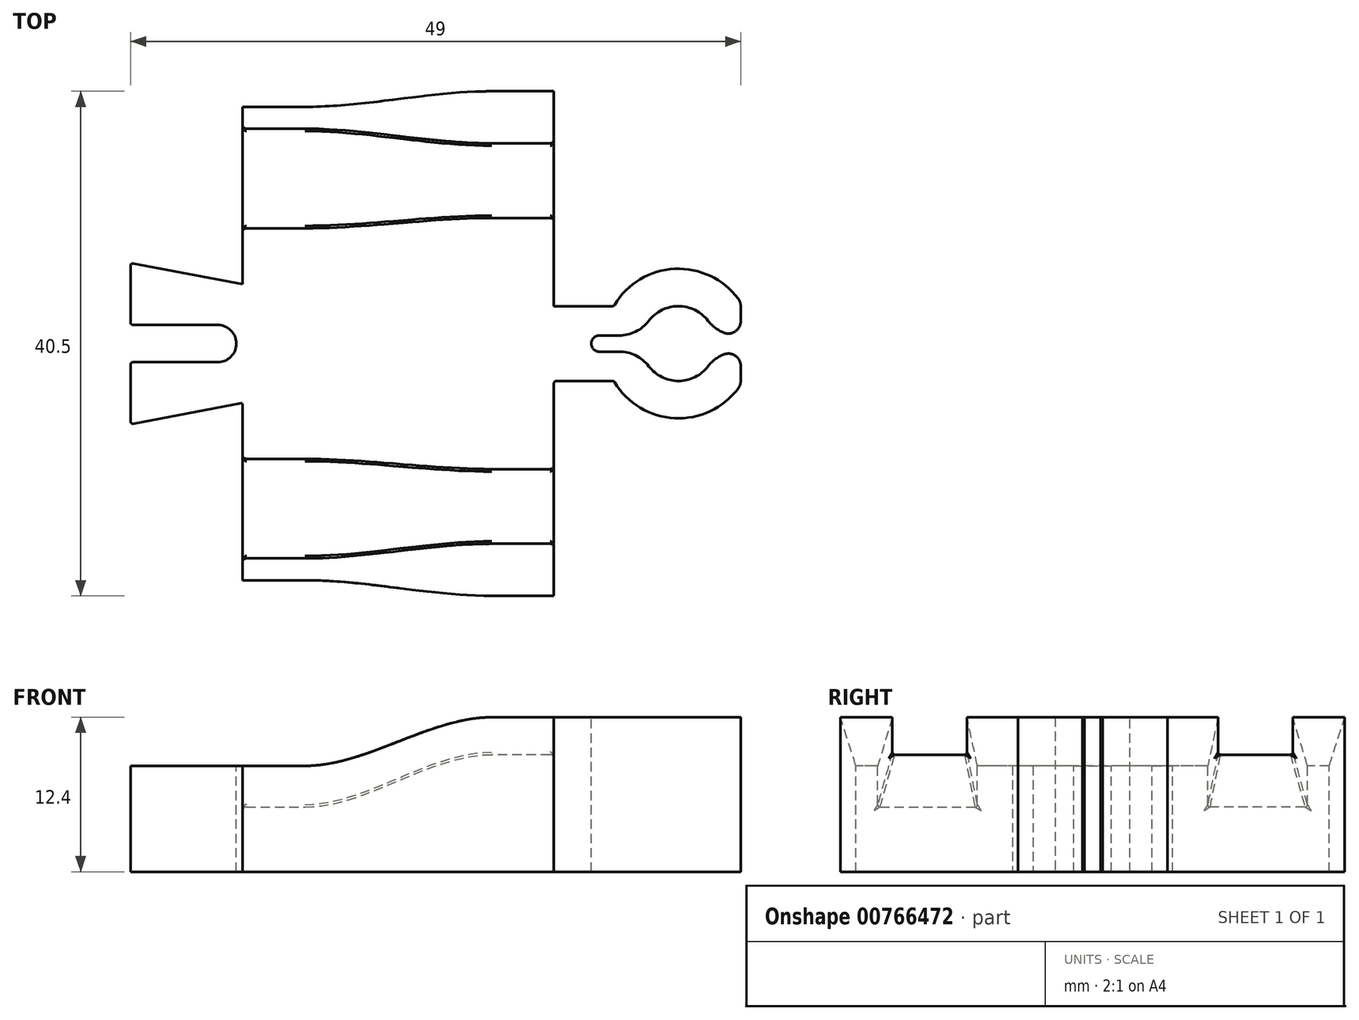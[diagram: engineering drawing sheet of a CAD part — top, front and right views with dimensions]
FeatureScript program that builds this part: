
annotation { "Feature Type Name" : "Feature", "Feature Type Description" : "" }
export const myFeature = defineFeature(function(context is Context, id is Id, definition is map)
    precondition{}
    {
        {
            var Q0;
            Q0=qCreatedBy(makeId("Right.planeOp"),FACE);
            cPlane(context, id + "F0", {"entities" : qUnion([Q0]), "cplaneType" : CPlaneType.OFFSET, "offset" : 15 * mm, "width" : 150 * mm, "height" : 150 * mm});
        }
        {
            var Q0;
            Q0=qCreatedBy(makeId("Right.planeOp"),FACE);
            var sketch = newSketch(context, id + "F1", { "sketchPlane" : qUnion([Q0])});
            skLineSegment(sketch, "E0.bottom", {"start": v(19, 0) * mm, "end": v(-19, 0) * mm});
            skLineSegment(sketch, "E0.top", {"start": v(19, 8.5) * mm, "end": v(17.25, 8.5) * mm});
            skLineSegment(sketch, "E0.left", {"start": v(19, 0) * mm, "end": v(19, 8.5) * mm});
            skLineSegment(sketch, "E0.right", {"start": v(-19, 0) * mm, "end": v(-19, 8.5) * mm});
            skPoint(sketch, "E0.middle", {"position": v(0, 4.25) * mm});
            skLineSegment(sketch, "E1.bottom", {"start": v(17.25, 5.2) * mm, "end": v(9.25, 5.2) * mm});
            skLineSegment(sketch, "E1.left", {"start": v(17.25, 5.2) * mm, "end": v(17.25, 8.5) * mm});
            skLineSegment(sketch, "E1.right", {"start": v(9.25, 5.2) * mm, "end": v(9.25, 8.5) * mm});
            skPoint(sketch, "E1.middle", {"position": v(13.25, 12.03) * mm});
            skPoint(sketch, "E2.orphan", {"position": v(9.25, 18.86) * mm});
            skPoint(sketch, "E3.orphan", {"position": v(17.25, 18.86) * mm});
            skLineSegment(sketch, "E4.trimOffspring", {"start": v(9.25, 8.5) * mm, "end": v(-9.25, 8.5) * mm});
            skLineSegment(sketch, "E5.MirrorCS", {"start": v(-9.25, 5.2) * mm, "end": v(-9.25, 8.5) * mm});
            skLineSegment(sketch, "E6.MirrorCS", {"start": v(-17.25, 5.2) * mm, "end": v(-9.25, 5.2) * mm});
            skLineSegment(sketch, "E7.MirrorCS", {"start": v(-17.25, 5.2) * mm, "end": v(-17.25, 8.5) * mm});
            skLineSegment(sketch, "E8.trimOffspring", {"start": v(-17.25, 8.5) * mm, "end": v(-19, 8.5) * mm});
            skSolve(sketch);
        }
        {
            var Q0;
            Q0=makeQuery(id+"F1.imprint","IMPRINT",FACE,{"disambiguationData":[TD([[makeQuery(id+"F1.imprint","IMPRINT",EDGE,{"derivedFrom":sQuery(id+"F1.wireOp",EDGE,"E0.bottom")}),-1.0]])]});
            extrude(context, id + "F2", {"entities" : qUnion([Q0]), "oppositeDirection" : true, "depth" : 5 * mm, "offsetDistance" : 25 * mm});
        }
        {
            var Q0;
            Q0=qCreatedBy(id+"F0.planeOp",FACE);
            var sketch = newSketch(context, id + "F3", { "sketchPlane" : qUnion([Q0])});
            skLineSegment(sketch, "E9.bottom", {"start": v(20.25, 0) * mm, "end": v(-20.25, 0) * mm});
            skLineSegment(sketch, "E9.top", {"start": v(20.25, 12.4) * mm, "end": v(16.07, 12.4) * mm});
            skLineSegment(sketch, "E9.left", {"start": v(20.25, 0) * mm, "end": v(20.25, 12.4) * mm});
            skLineSegment(sketch, "E9.right", {"start": v(-20.25, 0) * mm, "end": v(-20.25, 12.4) * mm});
            skPoint(sketch, "E9.middle", {"position": v(0, 6.2) * mm});
            skLineSegment(sketch, "E10.bottom", {"start": v(16.07, 9.4) * mm, "end": v(10.07, 9.4) * mm});
            skLineSegment(sketch, "E10.left", {"start": v(16.07, 9.4) * mm, "end": v(16.07, 12.4) * mm});
            skLineSegment(sketch, "E10.right", {"start": v(10.07, 9.4) * mm, "end": v(10.07, 12.4) * mm});
            skPoint(sketch, "E10.middle", {"position": v(13.07, 12.4) * mm});
            skPoint(sketch, "E11.orphan", {"position": v(10.07, 15.41) * mm});
            skLineSegment(sketch, "E12.trimOffspring", {"start": v(10.08, 12.4) * mm, "end": v(-10.08, 12.4) * mm});
            skPoint(sketch, "E13.orphan", {"position": v(16.07, 15.41) * mm});
            skLineSegment(sketch, "E14.MirrorCS", {"start": v(-10.08, 9.4) * mm, "end": v(-10.08, 12.4) * mm});
            skLineSegment(sketch, "E15.MirrorCS", {"start": v(-16.07, 9.4) * mm, "end": v(-10.07, 9.4) * mm});
            skLineSegment(sketch, "E16.MirrorCS", {"start": v(-16.07, 9.4) * mm, "end": v(-16.07, 12.4) * mm});
            skLineSegment(sketch, "E17.trimOffspring", {"start": v(-16.07, 12.4) * mm, "end": v(-20.25, 12.4) * mm});
            skSolve(sketch);
        }
        {
            var Q0;
            Q0 = qSketchRegion(id + "F3", true);
            extrude(context, id + "F4", {"entities" : qUnion([Q0]), "depth" : 5 * mm, "offsetDistance" : 25 * mm});
        }
        {
            var Q0;
            Q0=makeQuery(id+"F4.opExtrude","CAP_FACE",FACE,{"disambiguationData":[OSD([sQuery(id+"F3.wireOp",EDGE,"E9.bottom"),sQuery(id+"F3.wireOp",EDGE,"E9.top"),sQuery(id+"F3.wireOp",EDGE,"E9.left"),sQuery(id+"F3.wireOp",EDGE,"E9.right"),sQuery(id+"F3.wireOp",EDGE,"E10.bottom"),sQuery(id+"F3.wireOp",EDGE,"E10.left"),sQuery(id+"F3.wireOp",EDGE,"E10.right"),sQuery(id+"F3.wireOp",EDGE,"E12.trimOffspring"),sQuery(id+"F3.wireOp",EDGE,"E14.MirrorCS"),sQuery(id+"F3.wireOp",EDGE,"E15.MirrorCS"),sQuery(id+"F3.wireOp",EDGE,"E16.MirrorCS"),sQuery(id+"F3.wireOp",EDGE,"E17.trimOffspring")])],"isStart":true});
            var Q1;
            Q1=makeQuery(id+"F2.opExtrude","CAP_FACE",FACE,{"disambiguationData":[OSD([sQuery(id+"F1.wireOp",EDGE,"E0.bottom"),sQuery(id+"F1.wireOp",EDGE,"E0.top"),sQuery(id+"F1.wireOp",EDGE,"E0.left"),sQuery(id+"F1.wireOp",EDGE,"E0.right"),sQuery(id+"F1.wireOp",EDGE,"E1.bottom"),sQuery(id+"F1.wireOp",EDGE,"E1.left"),sQuery(id+"F1.wireOp",EDGE,"E1.right"),sQuery(id+"F1.wireOp",EDGE,"E4.trimOffspring"),sQuery(id+"F1.wireOp",EDGE,"E5.MirrorCS"),sQuery(id+"F1.wireOp",EDGE,"E6.MirrorCS"),sQuery(id+"F1.wireOp",EDGE,"E7.MirrorCS"),sQuery(id+"F1.wireOp",EDGE,"E8.trimOffspring")])],"isStart":true});
            loft(context, id + "F5", {"operationType" : NewBodyOperationType.ADD, "startCondition" : LoftEndDerivativeType.NORMAL_TO_PROFILE, "startMagnitude" : 1, "endCondition" : LoftEndDerivativeType.NORMAL_TO_PROFILE, "endMagnitude" : 1, "sheetProfilesArray" : [{ "sheetProfileEntities" : qUnion([Q0]) }, { "sheetProfileEntities" : qUnion([Q1]) }]});
        }
        {
            var Q0;
            Q0=makeQuery(id+"F2.opExtrude","SWEPT_FACE",FACE,{"disambiguationData":[OSD([sQuery(id+"F1.wireOp",EDGE,"E4.trimOffspring")])]});
            var sketch = newSketch(context, id + "F6", { "sketchPlane" : qUnion([Q0])});
            skLineSegment(sketch, "E18.0", {"start": v(-5, 4.78) * mm, "end": v(-5, -4.78) * mm});
            skLineSegment(sketch, "E19", {"start": v(-5, 4.78) * mm, "end": v(-14, 6.47) * mm});
            skLineSegment(sketch, "E20", {"start": v(-5, 0) * mm, "end": v(-14, 0) * mm, "construction": true});
            skLineSegment(sketch, "E21.MirrorCS", {"start": v(-5, -4.78) * mm, "end": v(-14, -6.47) * mm});
            skLineSegment(sketch, "E22", {"start": v(-14, 6.47) * mm, "end": v(-14, 1.5) * mm});
            skPoint(sketch, "E23.orphan", {"position": v(-5, 9.25) * mm});
            skPoint(sketch, "E24.orphan", {"position": v(-5, -9.25) * mm});
            skLineSegment(sketch, "E25.bottom", {"start": v(-7, 1.5) * mm, "end": v(-14, 1.5) * mm});
            skLineSegment(sketch, "E25.top", {"start": v(-7, -1.5) * mm, "end": v(-14, -1.5) * mm});
            skPoint(sketch, "E25.middle", {"position": v(-15.83, 0) * mm});
            skArc(sketch, "E26", {"start": v(-7, -1.5) * mm, "mid": v(-5.5, 0) * mm, "end": v(-7, 1.5) * mm});
            skPoint(sketch, "E27.orphan", {"position": v(-22.96, 1.5) * mm});
            skPoint(sketch, "E28.orphan", {"position": v(-32.28, -1.5) * mm});
            skPoint(sketch, "E29.orphan", {"position": v(-8.7, -1.5) * mm});
            skPoint(sketch, "E30.orphan", {"position": v(0.6, 1.5) * mm});
            skLineSegment(sketch, "E31.trimOffspring", {"start": v(-14, -1.5) * mm, "end": v(-14, -6.47) * mm});
            skSolve(sketch);
        }
        {
            var Q0;
            Q0=makeQuery(id+"F6.imprint","IMPRINT",FACE,{"disambiguationData":[TD([[makeQuery(id+"F6.imprint","IMPRINT",EDGE,{"derivedFrom":sQuery(id+"F6.wireOp",EDGE,"E18.0")}),-1.0]])]});
            var Q1;
            {var subQ0=sQuery(id+"F3.wireOp",EDGE,"E9.bottom");var subQ1=sQuery(id+"F1.wireOp",EDGE,"E0.bottom");Q1=makeQuery(id+"F5.boolean.opBoolean","MERGE",FACE,{"derivedFrom":[makeQuery(id+"F2.opExtrude","SWEPT_FACE",FACE,{"disambiguationData":[OSD([subQ1])]}),makeQuery(id+"F4.opExtrude","SWEPT_FACE",FACE,{"disambiguationData":[OSD([subQ0])]}),makeQuery(id+"F5.opLoft","SWEPT_FACE",FACE,{"disambiguationData":[OSD([subQ1,sQuery(id+"F1.wireOp",EDGE,"E0.left"),sQuery(id+"F1.wireOp",EDGE,"E0.right"),subQ0,sQuery(id+"F3.wireOp",EDGE,"E9.left"),sQuery(id+"F3.wireOp",EDGE,"E9.right")])]})]});}
            extrude(context, id + "F7", {"entities" : qUnion([Q0]), "operationType" : NewBodyOperationType.ADD, "endBound" : BoundingType.UP_TO_SURFACE, "oppositeDirection" : true, "depth" : 25 * mm, "endBoundEntityFace" : qUnion([Q1]), "offsetDistance" : 25 * mm});
        }
        {
            var Q0;
            Q0=makeQuery(id+"F7.opExtrude","SWEPT_EDGE",EDGE,{"disambiguationData":[OSD([sQuery(id+"F6.wireOp",EDGE,"E19"),sQuery(id+"F6.wireOp",EDGE,"E22")])]});
            var Q1;
            Q1=makeQuery(id+"F7.opExtrude","SWEPT_EDGE",EDGE,{"disambiguationData":[OSD([sQuery(id+"F6.wireOp",EDGE,"E21.MirrorCS"),sQuery(id+"F6.wireOp",EDGE,"E31.trimOffspring")])]});
            var Q2;
            Q2=makeQuery(id+"F7.opExtrude","SWEPT_EDGE",EDGE,{"disambiguationData":[OSD([sQuery(id+"F6.wireOp",EDGE,"E22"),sQuery(id+"F6.wireOp",EDGE,"E25.bottom")])]});
            var Q3;
            Q3=makeQuery(id+"F7.opExtrude","SWEPT_EDGE",EDGE,{"disambiguationData":[OSD([sQuery(id+"F6.wireOp",EDGE,"E25.top"),sQuery(id+"F6.wireOp",EDGE,"E31.trimOffspring")])]});
            fillet(context, id + "F8", {"entities" : qUnion([Q0, Q1, Q2, Q3]), "radius" : 0.2 * mm, "tangentPropagation" : true, "allowEdgeOverflow" : false});
        }
        {
            var Q0;
            Q0=makeQuery(id+"F7.opExtrude","SWEPT_EDGE",EDGE,{"disambiguationData":[OSD([sQuery(id+"F1.wireOp",EDGE,"E4.trimOffspring"),sQuery(id+"F6.wireOp",EDGE,"E18.0"),sQuery(id+"F6.wireOp",EDGE,"E19")])]});
            var Q1;
            Q1=makeQuery(id+"F7.opExtrude","SWEPT_EDGE",EDGE,{"disambiguationData":[OSD([sQuery(id+"F1.wireOp",EDGE,"E4.trimOffspring"),sQuery(id+"F6.wireOp",EDGE,"E18.0"),sQuery(id+"F6.wireOp",EDGE,"E21.MirrorCS")])]});
            fillet(context, id + "F9", {"entities" : qUnion([Q0, Q1]), "radius" : 0.1 * mm, "tangentPropagation" : true, "allowEdgeOverflow" : false});
        }
        {
            var Q0;
            Q0=makeQuery(id+"F4.opExtrude","SWEPT_FACE",FACE,{"disambiguationData":[OSD([sQuery(id+"F3.wireOp",EDGE,"E12.trimOffspring")])]});
            var sketch = newSketch(context, id + "F10", { "sketchPlane" : qUnion([Q0])});
            skLineSegment(sketch, "E32.0", {"start": v(20, 10.07) * mm, "end": v(20, -10.08) * mm, "construction": true});
            skLineSegment(sketch, "E33.bottom", {"start": v(20, 3) * mm, "end": v(24.8, 3) * mm});
            skLineSegment(sketch, "E33.top", {"start": v(20, -3) * mm, "end": v(24.8, -3) * mm});
            skLineSegment(sketch, "E33.left", {"start": v(20, 3) * mm, "end": v(20, -3) * mm});
            skPoint(sketch, "E33.middle", {"position": v(23.65, 0) * mm});
            skPoint(sketch, "E33.middle.positionSnap0", {"position": v(20, 0) * mm});
            skPoint(sketch, "E33.centerSnap0", {"position": v(20, 0) * mm});
            skArc(sketch, "E34", {"start": v(35, 3.32) * mm, "mid": v(29.81, 6) * mm, "end": v(24.8, 3) * mm});
            skLineSegment(sketch, "E35", {"start": v(35, 3.32) * mm, "end": v(35, 0.65) * mm});
            skPoint(sketch, "E36.orphan", {"position": v(27.3, 3) * mm});
            skPoint(sketch, "E37.orphan", {"position": v(27.3, -3) * mm});
            skArc(sketch, "E38.trimOffspring", {"start": v(24.8, -3) * mm, "mid": v(29.81, -6) * mm, "end": v(35, -3.32) * mm});
            skLineSegment(sketch, "E39.bottom", {"start": v(23.65, 0.65) * mm, "end": v(27.07, 0.65) * mm});
            skLineSegment(sketch, "E39.top", {"start": v(23.65, -0.65) * mm, "end": v(27.07, -0.65) * mm});
            skArc(sketch, "E40", {"start": v(23.65, 0.65) * mm, "mid": v(23, 0) * mm, "end": v(23.65, -0.65) * mm});
            skPoint(sketch, "E39.left.start.orphan", {"position": v(25, 0.65) * mm});
            skPoint(sketch, "E41.orphan", {"position": v(25, -0.65) * mm});
            skLineSegment(sketch, "E42.trimOffspring", {"start": v(35, -0.65) * mm, "end": v(35, -3.46) * mm});
            skPoint(sketch, "E39.right.end.orphan", {"position": v(35, -0.65) * mm});
            skPoint(sketch, "E39.right.start.orphan", {"position": v(35, 0.65) * mm});
            skArc(sketch, "E43", {"start": v(32.93, 0.65) * mm, "mid": v(30, 3) * mm, "end": v(27.07, 0.65) * mm});
            skLineSegment(sketch, "E44.trimOffspring", {"start": v(32.93, -0.65) * mm, "end": v(35, -0.65) * mm});
            skLineSegment(sketch, "E45.trimOffspring", {"start": v(32.93, 0.65) * mm, "end": v(35, 0.65) * mm});
            skArc(sketch, "E46.trimOffspring", {"start": v(27.07, -0.65) * mm, "mid": v(30, -3) * mm, "end": v(32.93, -0.65) * mm});
            skSolve(sketch);
        }
        {
            var Q0;
            Q0=makeQuery(id+"F10.imprint","IMPRINT",FACE,{"disambiguationData":[TD([[makeQuery(id+"F10.imprint","IMPRINT",EDGE,{"derivedFrom":sQuery(id+"F10.wireOp",EDGE,"E33.bottom")}),-1.0]])]});
            var Q1;
            {var subQ0=sQuery(id+"F3.wireOp",EDGE,"E9.right");var subQ1=sQuery(id+"F3.wireOp",EDGE,"E9.left");var subQ2=sQuery(id+"F3.wireOp",EDGE,"E9.bottom");var subQ3=sQuery(id+"F1.wireOp",EDGE,"E0.right");var subQ4=sQuery(id+"F1.wireOp",EDGE,"E0.left");var subQ5=sQuery(id+"F1.wireOp",EDGE,"E0.bottom");Q1=makeQuery(id+"F7.boolean.opBoolean","MERGE",FACE,{"derivedFrom":[makeQuery(id+"F5.boolean.opBoolean","MERGE",FACE,{"derivedFrom":[makeQuery(id+"F2.opExtrude","SWEPT_FACE",FACE,{"disambiguationData":[OSD([subQ5])]}),makeQuery(id+"F4.opExtrude","SWEPT_FACE",FACE,{"disambiguationData":[OSD([subQ2])]}),makeQuery(id+"F5.opLoft","SWEPT_FACE",FACE,{"disambiguationData":[OSD([subQ5,subQ4,subQ3,subQ2,subQ1,subQ0])]})]}),makeQuery(id+"F7.opExtrude","CAP_FACE",FACE,{"disambiguationData":[OSD([subQ5,subQ4,subQ3,subQ2,subQ1,subQ0])],"isStart":false})]});}
            extrude(context, id + "F11", {"entities" : qUnion([Q0]), "operationType" : NewBodyOperationType.ADD, "endBound" : BoundingType.UP_TO_SURFACE, "oppositeDirection" : true, "depth" : 25 * mm, "endBoundEntityFace" : qUnion([Q1]), "offsetDistance" : 25 * mm});
        }
        {
            var Q0;
            Q0=makeQuery(id+"F11.opExtrude","SWEPT_EDGE",EDGE,{"disambiguationData":[OSD([sQuery(id+"F10.wireOp",EDGE,"E39.bottom"),sQuery(id+"F10.wireOp",EDGE,"E43")])]});
            var Q1;
            Q1=makeQuery(id+"F11.opExtrude","SWEPT_EDGE",EDGE,{"disambiguationData":[OSD([sQuery(id+"F10.wireOp",EDGE,"E39.top"),sQuery(id+"F10.wireOp",EDGE,"E46.trimOffspring")])]});
            var Q2;
            Q2=makeQuery(id+"F11.opExtrude","SWEPT_EDGE",EDGE,{"disambiguationData":[OSD([sQuery(id+"F10.wireOp",EDGE,"E43"),sQuery(id+"F10.wireOp",EDGE,"E45.trimOffspring")])]});
            var Q3;
            Q3=makeQuery(id+"F11.opExtrude","SWEPT_EDGE",EDGE,{"disambiguationData":[OSD([sQuery(id+"F10.wireOp",EDGE,"E44.trimOffspring"),sQuery(id+"F10.wireOp",EDGE,"E46.trimOffspring")])]});
            fillet(context, id + "F12", {"entities" : qUnion([Q0, Q1, Q2, Q3]), "radius" : 3 * mm, "tangentPropagation" : true, "allowEdgeOverflow" : false});
        }
        {
            var Q0;
            Q0=makeQuery(id+"F11.opExtrude","SWEPT_EDGE",EDGE,{"disambiguationData":[OSD([sQuery(id+"F10.wireOp",EDGE,"E34"),sQuery(id+"F10.wireOp",EDGE,"E35")])]});
            var Q1;
            Q1=makeQuery(id+"F11.opExtrude","SWEPT_EDGE",EDGE,{"disambiguationData":[OSD([sQuery(id+"F10.wireOp",EDGE,"E35"),sQuery(id+"F10.wireOp",EDGE,"E45.trimOffspring")])]});
            var Q2;
            Q2=makeQuery(id+"F11.opExtrude","SWEPT_EDGE",EDGE,{"disambiguationData":[OSD([sQuery(id+"F10.wireOp",EDGE,"E42.trimOffspring"),sQuery(id+"F10.wireOp",EDGE,"E44.trimOffspring")])]});
            var Q3;
            Q3=makeQuery(id+"F11.opExtrude","SWEPT_EDGE",EDGE,{"disambiguationData":[OSD([sQuery(id+"F10.wireOp",EDGE,"E38.trimOffspring"),sQuery(id+"F10.wireOp",EDGE,"E42.trimOffspring")])]});
            fillet(context, id + "F13", {"entities" : qUnion([Q0, Q1, Q2, Q3]), "radius" : 1 * mm, "tangentPropagation" : true, "allowEdgeOverflow" : false});
        }
        {
            var Q0;
            Q0=makeQuery(id+"F11.opExtrude","SWEPT_EDGE",EDGE,{"disambiguationData":[OSD([sQuery(id+"F3.wireOp",EDGE,"E12.trimOffspring"),sQuery(id+"F10.wireOp",EDGE,"E33.top"),sQuery(id+"F10.wireOp",EDGE,"E33.left")])]});
            var Q1;
            Q1=makeQuery(id+"F11.opExtrude","SWEPT_EDGE",EDGE,{"disambiguationData":[OSD([sQuery(id+"F10.wireOp",EDGE,"E33.top"),sQuery(id+"F10.wireOp",EDGE,"E38.trimOffspring")])]});
            var Q2;
            Q2=makeQuery(id+"F11.opExtrude","SWEPT_EDGE",EDGE,{"disambiguationData":[OSD([sQuery(id+"F3.wireOp",EDGE,"E12.trimOffspring"),sQuery(id+"F10.wireOp",EDGE,"E33.bottom"),sQuery(id+"F10.wireOp",EDGE,"E33.left")])]});
            var Q3;
            Q3=makeQuery(id+"F11.opExtrude","SWEPT_EDGE",EDGE,{"disambiguationData":[OSD([sQuery(id+"F10.wireOp",EDGE,"E33.bottom"),sQuery(id+"F10.wireOp",EDGE,"E34")])]});
            fillet(context, id + "F14", {"entities" : qUnion([Q0, Q1, Q2, Q3]), "radius" : 0.2 * mm, "tangentPropagation" : true, "allowEdgeOverflow" : false});
        }
        {
            var Q0;
            Q0=makeQuery(id+"F2.opExtrude","CAP_EDGE",EDGE,{"disambiguationData":[OSD([sQuery(id+"F1.wireOp",EDGE,"E1.left")])],"isStart":false});
            var Q1;
            Q1=makeQuery(id+"F2.opExtrude","CAP_EDGE",EDGE,{"disambiguationData":[OSD([sQuery(id+"F1.wireOp",EDGE,"E1.right")])],"isStart":false});
            var Q2;
            Q2=makeQuery(id+"F2.opExtrude","CAP_EDGE",EDGE,{"disambiguationData":[OSD([sQuery(id+"F1.wireOp",EDGE,"E1.bottom")])],"isStart":false});
            var Q3;
            Q3=makeQuery(id+"F2.opExtrude","CAP_EDGE",EDGE,{"disambiguationData":[OSD([sQuery(id+"F1.wireOp",EDGE,"E5.MirrorCS")])],"isStart":false});
            var Q4;
            Q4=makeQuery(id+"F2.opExtrude","CAP_EDGE",EDGE,{"disambiguationData":[OSD([sQuery(id+"F1.wireOp",EDGE,"E6.MirrorCS")])],"isStart":false});
            var Q5;
            Q5=makeQuery(id+"F2.opExtrude","CAP_EDGE",EDGE,{"disambiguationData":[OSD([sQuery(id+"F1.wireOp",EDGE,"E7.MirrorCS")])],"isStart":false});
            var Q6;
            Q6=makeQuery(id+"F4.opExtrude","CAP_EDGE",EDGE,{"disambiguationData":[OSD([sQuery(id+"F3.wireOp",EDGE,"E16.MirrorCS")])],"isStart":false});
            var Q7;
            Q7=makeQuery(id+"F4.opExtrude","CAP_EDGE",EDGE,{"disambiguationData":[OSD([sQuery(id+"F3.wireOp",EDGE,"E15.MirrorCS")])],"isStart":false});
            var Q8;
            Q8=makeQuery(id+"F4.opExtrude","CAP_EDGE",EDGE,{"disambiguationData":[OSD([sQuery(id+"F3.wireOp",EDGE,"E14.MirrorCS")])],"isStart":false});
            var Q9;
            Q9=makeQuery(id+"F4.opExtrude","CAP_EDGE",EDGE,{"disambiguationData":[OSD([sQuery(id+"F3.wireOp",EDGE,"E10.left")])],"isStart":false});
            var Q10;
            Q10=makeQuery(id+"F4.opExtrude","CAP_EDGE",EDGE,{"disambiguationData":[OSD([sQuery(id+"F3.wireOp",EDGE,"E10.bottom")])],"isStart":false});
            var Q11;
            Q11=makeQuery(id+"F4.opExtrude","CAP_EDGE",EDGE,{"disambiguationData":[OSD([sQuery(id+"F3.wireOp",EDGE,"E10.right")])],"isStart":false});
            fillet(context, id + "F15", {"entities" : qUnion([Q0, Q1, Q2, Q3, Q4, Q5, Q6, Q7, Q8, Q9, Q10, Q11]), "radius" : 0.3 * mm, "tangentPropagation" : true, "allowEdgeOverflow" : false});
        }
        {
            var Q0;
            Q0=makeQuery(id+"F5.opLoft","SWEPT_EDGE",EDGE,{"disambiguationData":[OSD([sQuery(id+"F1.wireOp",EDGE,"E1.bottom"),sQuery(id+"F1.wireOp",EDGE,"E1.left"),sQuery(id+"F3.wireOp",EDGE,"E10.bottom"),sQuery(id+"F3.wireOp",EDGE,"E10.left")])]});
            var Q1;
            Q1=makeQuery(id+"F5.opLoft","SWEPT_EDGE",EDGE,{"disambiguationData":[OSD([sQuery(id+"F1.wireOp",EDGE,"E1.bottom"),sQuery(id+"F1.wireOp",EDGE,"E1.right"),sQuery(id+"F3.wireOp",EDGE,"E10.bottom"),sQuery(id+"F3.wireOp",EDGE,"E10.right")])]});
            var Q2;
            Q2=makeQuery(id+"F5.opLoft","SWEPT_EDGE",EDGE,{"disambiguationData":[OSD([sQuery(id+"F1.wireOp",EDGE,"E6.MirrorCS"),sQuery(id+"F1.wireOp",EDGE,"E7.MirrorCS"),sQuery(id+"F3.wireOp",EDGE,"E15.MirrorCS"),sQuery(id+"F3.wireOp",EDGE,"E16.MirrorCS")])]});
            var Q3;
            Q3=makeQuery(id+"F5.opLoft","SWEPT_EDGE",EDGE,{"disambiguationData":[OSD([sQuery(id+"F1.wireOp",EDGE,"E5.MirrorCS"),sQuery(id+"F1.wireOp",EDGE,"E6.MirrorCS"),sQuery(id+"F3.wireOp",EDGE,"E14.MirrorCS"),sQuery(id+"F3.wireOp",EDGE,"E15.MirrorCS")])]});
            fillet(context, id + "F16", {"entities" : qUnion([Q0, Q1, Q2, Q3]), "radius" : 0.2 * mm, "tangentPropagation" : true, "allowEdgeOverflow" : false});
        }
    });
